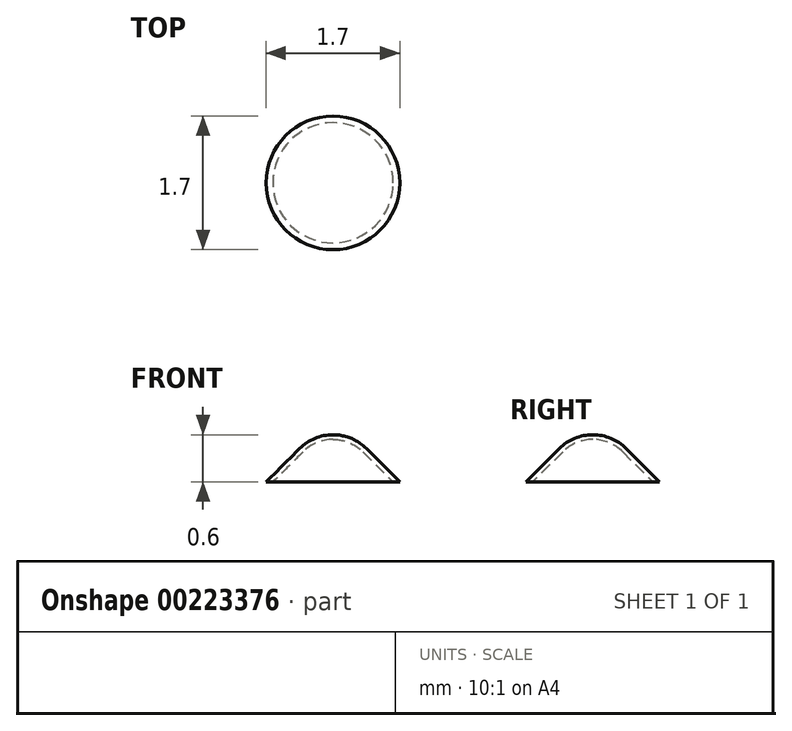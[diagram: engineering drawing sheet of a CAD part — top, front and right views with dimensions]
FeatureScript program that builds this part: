
annotation { "Feature Type Name" : "Feature", "Feature Type Description" : "" }
export const myFeature = defineFeature(function(context is Context, id is Id, definition is map)
    precondition{}
    {
        {
            var Q0;
            Q0=qCreatedBy(makeId("Front.planeOp"),FACE);
            var sketch = newSketch(context, id + "F0", { "sketchPlane" : qUnion([Q0])});
            skArc(sketch, "E0", {"start": v(0.6, 0) * mm, "mid": v(0.42, 0.42) * mm, "end": v(0, 0.6) * mm});
            skLineSegment(sketch, "E1", {"start": v(0, 0) * mm, "end": v(0.6, 0) * mm});
            skLineSegment(sketch, "E2", {"start": v(0, 0) * mm, "end": v(0, 0.6) * mm});
            skLineSegment(sketch, "E3", {"start": v(0, 0.85) * mm, "end": v(0.85, 0) * mm});
            skLineSegment(sketch, "E4", {"start": v(0, 0.85) * mm, "end": v(0, 0) * mm});
            skLineSegment(sketch, "E5", {"start": v(0.85, 0) * mm, "end": v(0, 0) * mm});
            skSolve(sketch);
        }
        {
            var Q0;
            Q0=makeQuery(id+"F0.imprint","IMPRINT",FACE,{"disambiguationData":[TD([[makeQuery(id+"F0.imprint","IMPRINT",EDGE,{"derivedFrom":sQuery(id+"F0.wireOp",EDGE,"E0")}),1.0]])]});
            var Q1;
            {var subQ0=sQuery(id+"F0.wireOp",EDGE,"E5");var subQ1=sQuery(id+"F0.wireOp",EDGE,"E0");var subQ2=makeQuery(id+"F0.imprint","INTERSECT",VERTEX,{"derivedFrom":[subQ1,subQ0]});Q1=makeQuery(id+"F0.imprint","IMPRINT",FACE,{"disambiguationData":[TD([[makeQuery(id+"F0.imprint","IMPRINT",EDGE,{"disambiguationData":[TD([[subQ2,-1.0]])],"derivedFrom":subQ1}),-1.0]])]});}
            var Q2;
            Q2=sQuery(id+"F0.wireOp",EDGE,"E2");
            revolve(context, id + "F1", {"entities" : qUnion([Q0, Q1]), "axis" : qUnion([Q2]), "revolveType" : RevolveType.FULL});
        }
        {
            var Q0;
            Q0=makeQuery(id+"F1.opRevolve","SWEPT_BODY",BODY,{"disambiguationData":[OSD([sQuery(id+"F0.wireOp",EDGE,"E0"),sQuery(id+"F0.wireOp",EDGE,"E3"),sQuery(id+"F0.wireOp",EDGE,"E4"),sQuery(id+"F0.wireOp",EDGE,"E5")])]});
            var Q1;
            Q1=sQuery(id+"F0.wireOp",VERTEX,"E0.center");
            transform(context, id + "F2", {"entities" : qUnion([Q0]), "transformType" : TransformType.SCALE_UNIFORMLY, "scale" : .9, "scalePoint" : qUnion([Q1]), "makeCopy" : true});
        }
    });
